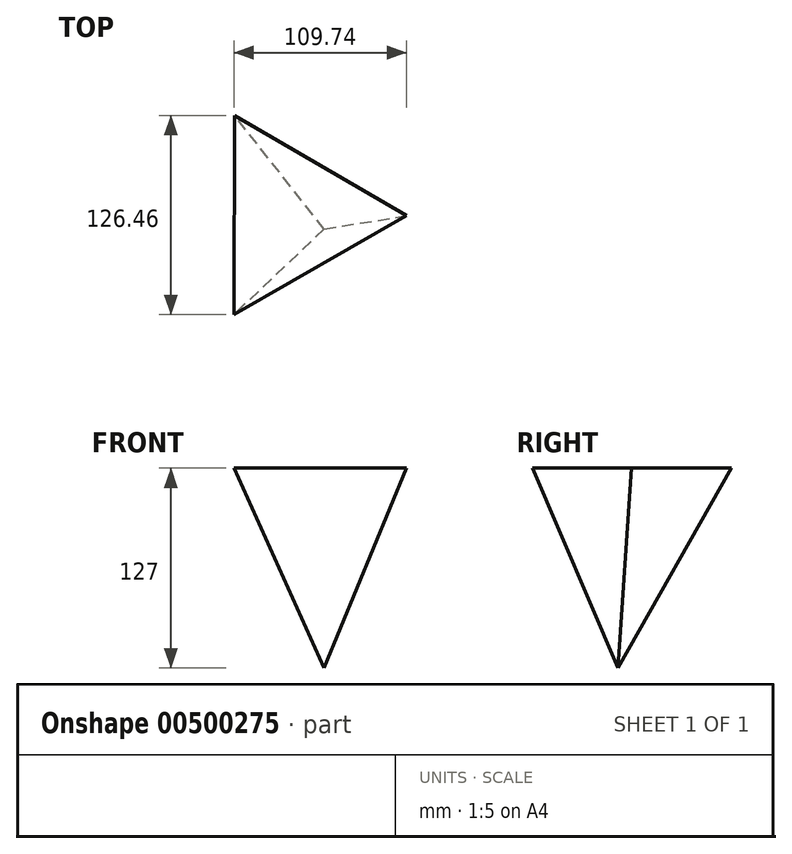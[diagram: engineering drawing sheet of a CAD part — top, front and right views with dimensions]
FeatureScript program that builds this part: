
annotation { "Feature Type Name" : "Feature", "Feature Type Description" : "" }
export const myFeature = defineFeature(function(context is Context, id is Id, definition is map)
    precondition{}
    {
        {
            var Q0;
            Q0=qCreatedBy(makeId("Top.planeOp"),FACE);
            var sketch = newSketch(context, id + "F0", { "sketchPlane" : qUnion([Q0])});
            skCircle(sketch, "E0.cCircle", {"center": v(0, 0) * mm, "radius": 73.01 * mm, "construction": true});
            skLineSegment(sketch, "E0.0", {"start": v(-36.73, -63.1) * mm, "end": v(-36.29, 63.36) * mm});
            skLineSegment(sketch, "E0.1", {"start": v(-36.29, 63.36) * mm, "end": v(73.01, -0.25) * mm});
            skLineSegment(sketch, "E0.2", {"start": v(73.01, -0.25) * mm, "end": v(-36.73, -63.1) * mm});
            skSolve(sketch);
        }
        {
            var Q0;
            Q0=qCreatedBy(makeId("Top.planeOp"),FACE);
            cPlane(context, id + "F1", {"entities" : qUnion([Q0]), "cplaneType" : CPlaneType.OFFSET, "offset" : 127 * mm, "oppositeDirection" : true, "width" : 152.4 * mm, "height" : 152.4 * mm});
        }
        {
            var Q0;
            Q0=qCreatedBy(id+"F1.planeOp",FACE);
            var sketch = newSketch(context, id + "F2", { "sketchPlane" : qUnion([Q0])});
            skPoint(sketch, "E1", {"position": v(20.68, -8.8) * mm});
            skSolve(sketch);
        }
        {
            var Q0;
            Q0=sQuery(id+"F2.wireOp",VERTEX,"E1");
            var Q1;
            Q1=makeQuery(id+"F0.imprint","IMPRINT",FACE,{"disambiguationData":[TD([[makeQuery(id+"F0.imprint","IMPRINT",EDGE,{"derivedFrom":sQuery(id+"F0.wireOp",EDGE,"E0.0")}),-1.0]])]});
            loft(context, id + "F3", {"sheetProfilesArray" : [{ "sheetProfileEntities" : qUnion([Q0]) }, { "sheetProfileEntities" : qUnion([Q1]) }]});
        }
    });
